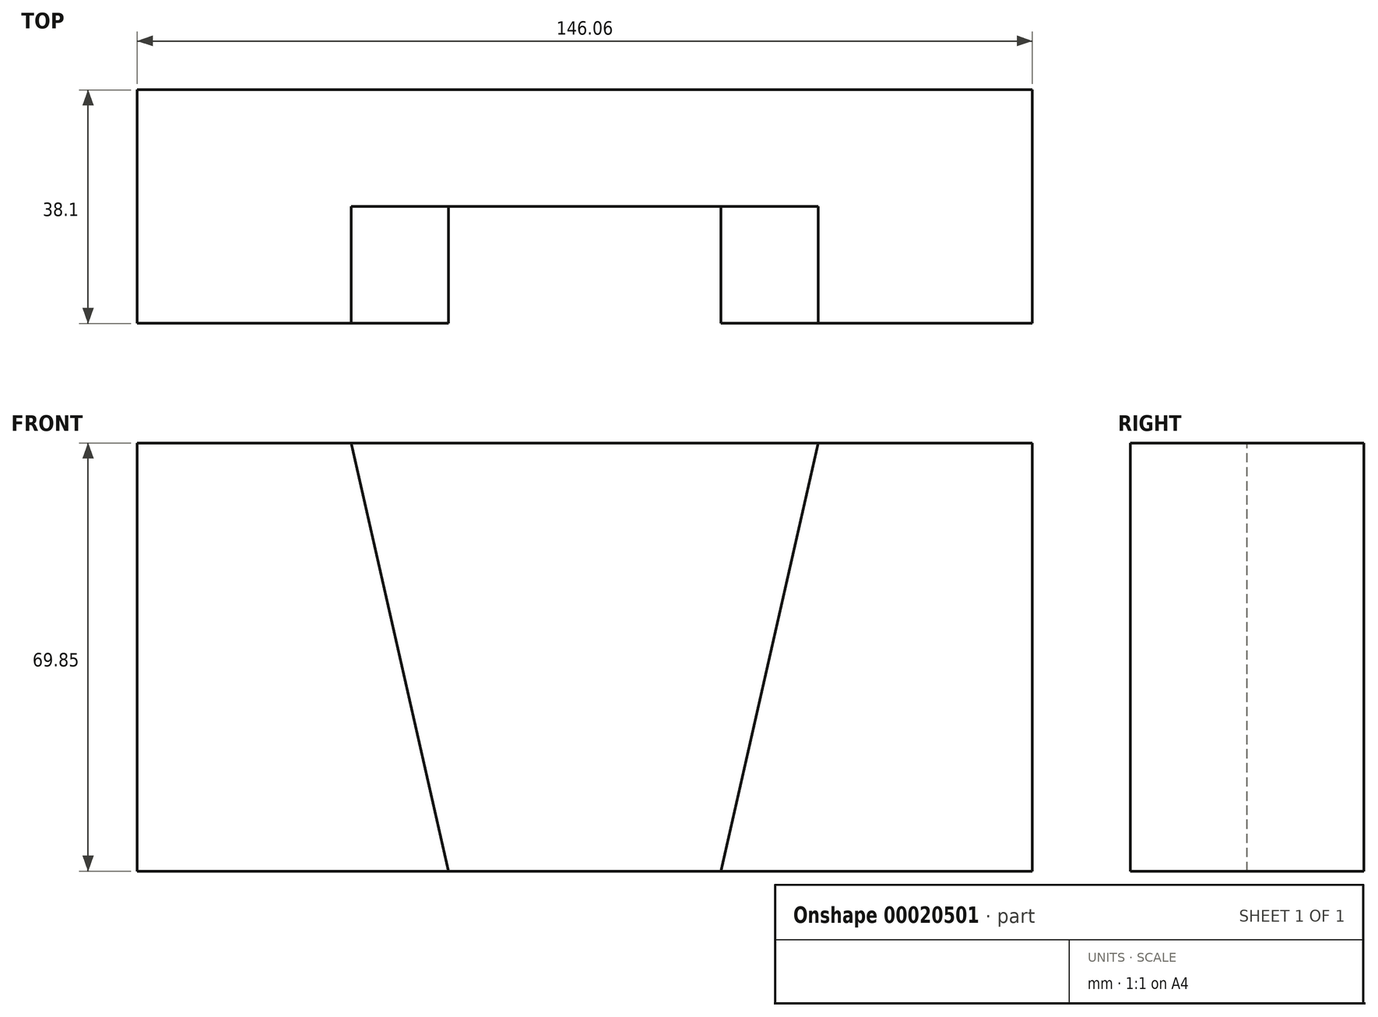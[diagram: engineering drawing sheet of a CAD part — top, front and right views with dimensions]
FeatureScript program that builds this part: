
annotation { "Feature Type Name" : "Feature", "Feature Type Description" : "" }
export const myFeature = defineFeature(function(context is Context, id is Id, definition is map)
    precondition{}
    {
        {
            var Q0;
            Q0=qCreatedBy(makeId("Top.planeOp"),FACE);
            var sketch = newSketch(context, id + "F0", { "sketchPlane" : qUnion([Q0])});
            skLineSegment(sketch, "E0.left", {"start": v(73.03, 35.05) * mm, "end": v(73.03, -3.05) * mm});
            skLineSegment(sketch, "E1", {"start": v(73.03, 35.05) * mm, "end": v(38.1, 35.05) * mm});
            skLineSegment(sketch, "E2", {"start": v(73.03, -3.05) * mm, "end": v(38.1, -3.05) * mm});
            skLineSegment(sketch, "E3", {"start": v(38.1, 35.05) * mm, "end": v(0, 35.05) * mm});
            skLineSegment(sketch, "E4", {"start": v(38.1, -3.05) * mm, "end": v(38.1, 16) * mm});
            skLineSegment(sketch, "E5", {"start": v(38.1, 16) * mm, "end": v(0, 16) * mm});
            skLineSegment(sketch, "E6", {"start": v(0, 35.05) * mm, "end": v(0, 16) * mm});
            skSolve(sketch);
        }
        {
            var Q0;
            Q0 = qSketchRegion(id + "F0", true);
            extrude(context, id + "F1", {"entities" : qUnion([Q0]), "depth" : 69.85 * mm});
        }
        {
            var Q0;
            Q0=makeQuery(id+"F1.opExtrude","SWEPT_FACE",FACE,{"disambiguationData":[OSD([sQuery(id+"F0.wireOp",EDGE,"E2")])]});
            var sketch = newSketch(context, id + "F2", { "sketchPlane" : qUnion([Q0])});
            skPoint(sketch, "E7.start.orphan", {"position": v(55.56, 69.85) * mm});
            skLineSegment(sketch, "E8", {"start": v(38.1, 0) * mm, "end": v(22.23, 0) * mm});
            skLineSegment(sketch, "E9", {"start": v(38.1, 69.85) * mm, "end": v(22.23, 0) * mm});
            skSolve(sketch);
        }
        {
            var Q0;
            Q0=makeQuery(id+"F2.imprint","IMPRINT",FACE,{"disambiguationData":[TD([[makeQuery(id+"F2.imprint","IMPRINT",EDGE,{"derivedFrom":sQuery(id+"F2.wireOp",EDGE,"E8")}),-1.0]])]});
            extrude(context, id + "F3", {"entities" : qUnion([Q0]), "operationType" : NewBodyOperationType.ADD, "depth" : 19.05 * mm, "hasSecondDirection" : true, "secondDirectionOppositeDirection" : true, "secondDirectionDepth" : 25.4 * mm});
        }
        {
            var Q0;
            Q0=makeQuery(id+"F3.opExtrude","CAP_FACE",FACE,{"disambiguationData":[OSD([sQuery(id+"F0.wireOp",EDGE,"E2"),sQuery(id+"F0.wireOp",EDGE,"E4"),sQuery(id+"F2.wireOp",EDGE,"E8"),sQuery(id+"F2.wireOp",EDGE,"E9")])],"isStart":false});
            extrude(context, id + "F4", {"entities" : qUnion([Q0]), "operationType" : NewBodyOperationType.REMOVE, "oppositeDirection" : true, "depth" : 25.4 * mm});
        }
        {
            var Q0;
            Q0=makeQuery(id+"F4.boolean.opBoolean","COPY",FACE,{"derivedFrom":makeQuery(id+"F4.opExtrude","CAP_FACE",FACE,{"disambiguationData":[OSD([sQuery(id+"F0.wireOp",EDGE,"E2"),sQuery(id+"F0.wireOp",EDGE,"E4"),sQuery(id+"F2.wireOp",EDGE,"E8"),sQuery(id+"F2.wireOp",EDGE,"E9")])],"isStart":false})});
            extrude(context, id + "F5", {"entities" : qUnion([Q0]), "operationType" : NewBodyOperationType.ADD, "depth" : 6.35 * mm});
        }
        {
            var Q0;
            Q0=makeQuery(id+"F1.opExtrude","SWEPT_BODY",BODY,{"disambiguationData":[OSD([sQuery(id+"F0.wireOp",EDGE,"E0.left"),sQuery(id+"F0.wireOp",EDGE,"E1"),sQuery(id+"F0.wireOp",EDGE,"E2"),sQuery(id+"F0.wireOp",EDGE,"E3"),sQuery(id+"F0.wireOp",EDGE,"E4"),sQuery(id+"F0.wireOp",EDGE,"E5"),sQuery(id+"F0.wireOp",EDGE,"E6")])]});
            var Q1;
            Q1=makeQuery(id+"F1.opExtrude","SWEPT_FACE",FACE,{"disambiguationData":[OSD([sQuery(id+"F0.wireOp",EDGE,"E6")])]});
            mirror(context, id + "F6", {"operationType" : NewBodyOperationType.ADD, "entities" : qUnion([Q0]), "mirrorPlane" : qUnion([Q1])});
        }
    });
